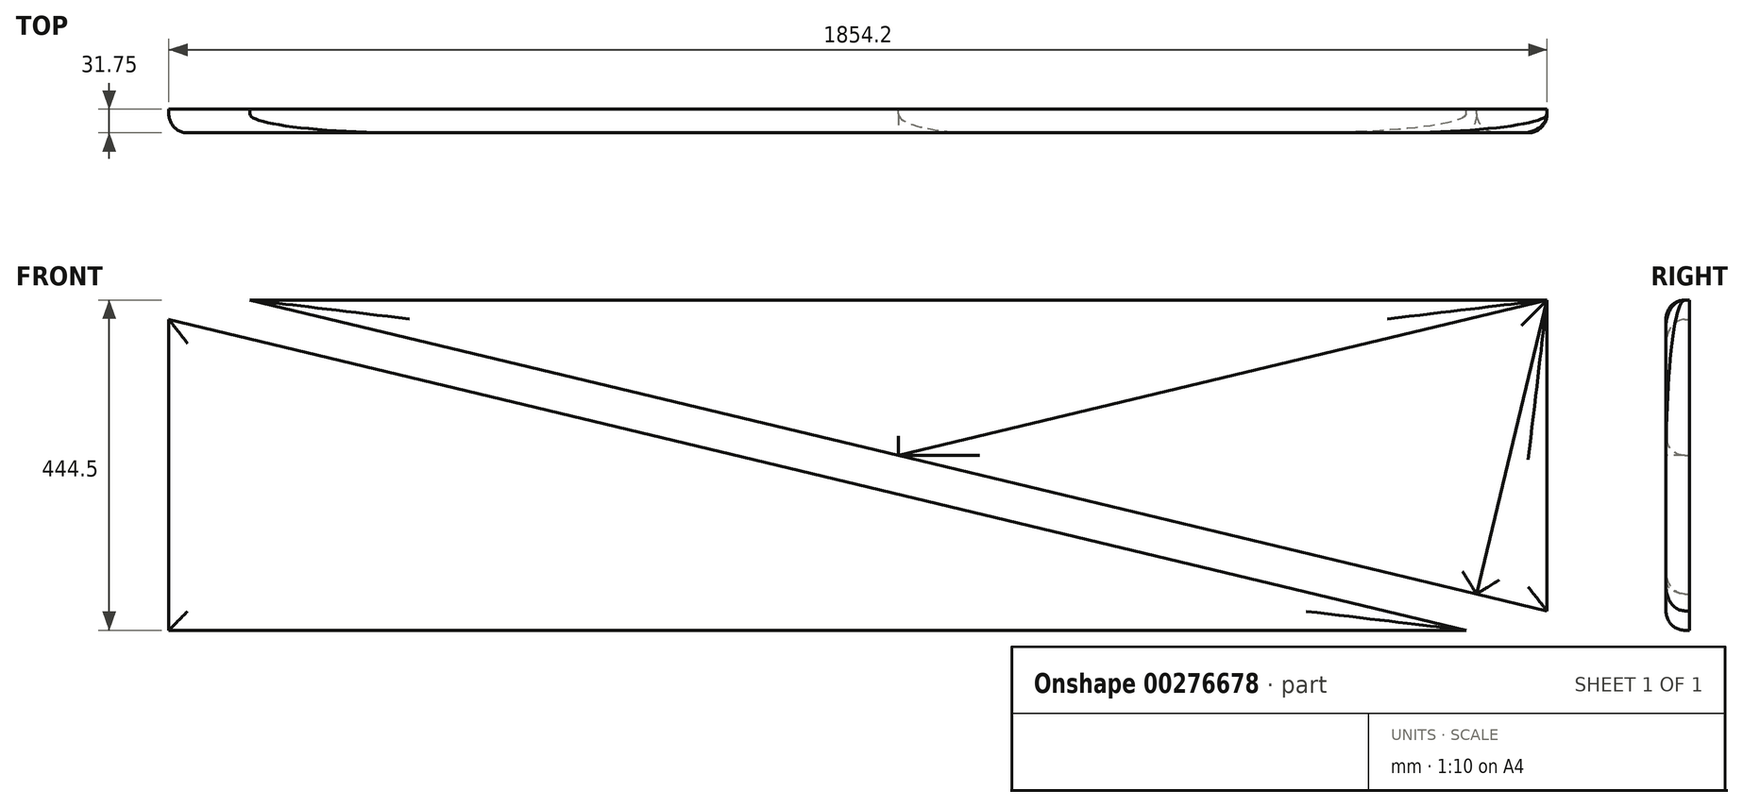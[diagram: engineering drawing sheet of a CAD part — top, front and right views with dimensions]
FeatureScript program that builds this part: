
annotation { "Feature Type Name" : "Feature", "Feature Type Description" : "" }
export const myFeature = defineFeature(function(context is Context, id is Id, definition is map)
    precondition{}
    {
        {
            var Q0;
            Q0=qCreatedBy(makeId("Front.planeOp"),FACE);
            var sketch = newSketch(context, id + "F0", { "sketchPlane" : qUnion([Q0])});
            skLineSegment(sketch, "E0.bottom", {"start": v(0, 0) * mm, "end": v(1854.2, 0) * mm});
            skLineSegment(sketch, "E0.top", {"start": v(0, 444.5) * mm, "end": v(1854.2, 444.5) * mm});
            skLineSegment(sketch, "E0.left", {"start": v(0, 0) * mm, "end": v(0, 444.5) * mm});
            skLineSegment(sketch, "E0.right", {"start": v(1854.2, 0) * mm, "end": v(1854.2, 444.5) * mm});
            skLineSegment(sketch, "E1", {"start": v(0, 444.5) * mm, "end": v(1854.2, 0) * mm});
            skLineSegment(sketch, "E2.0", {"start": v(0, 418.38) * mm, "end": v(1745.24, 0) * mm});
            skLineSegment(sketch, "E3.0", {"start": v(108.96, 444.5) * mm, "end": v(1854.2, 26.12) * mm});
            skLineSegment(sketch, "E4", {"start": v(1854.2, 444.5) * mm, "end": v(1759.35, 48.86) * mm});
            skLineSegment(sketch, "E5", {"start": v(1854.2, 444.5) * mm, "end": v(981.58, 235.3) * mm});
            skSolve(sketch);
        }
        {
            var Q0;
            {var subQ3=sQuery(id+"F0.wireOp",EDGE,"E2.0");Q0=makeQuery(id+"F0.imprint","IMPRINT",FACE,{"disambiguationData":[TD([[makeQuery(id+"F0.imprint","IMPRINT",EDGE,{"derivedFrom":subQ3}),-1.0]])]});}
            var Q1;
            {var subQ0=sQuery(id+"F0.wireOp",EDGE,"E5");Q1=makeQuery(id+"F0.imprint","IMPRINT",FACE,{"disambiguationData":[TD([[makeQuery(id+"F0.imprint","IMPRINT",EDGE,{"derivedFrom":subQ0}),-1.0]])]});}
            var Q2;
            {var subQ0=sQuery(id+"F0.wireOp",EDGE,"E4");Q2=makeQuery(id+"F0.imprint","IMPRINT",FACE,{"disambiguationData":[TD([[makeQuery(id+"F0.imprint","IMPRINT",EDGE,{"derivedFrom":subQ0}),1.0]])]});}
            extrude(context, id + "F1", {"entities" : qUnion([Q0, Q1, Q2]), "depth" : 31.75 * mm});
        }
        {
            var Q0;
            Q0=makeQuery(id+"F1.opExtrude","CAP_FACE",FACE,{"disambiguationData":[OSD([sQuery(id+"F0.wireOp",EDGE,"E0.bottom"),sQuery(id+"F0.wireOp",EDGE,"E0.left"),sQuery(id+"F0.wireOp",EDGE,"E2.0")])],"isStart":false});
            fillet(context, id + "F2", {"entities" : qUnion([Q0]), "radius" : 25.4 * mm, "tangentPropagation" : true, "allowEdgeOverflow" : false});
        }
        {
            var Q0;
            Q0=makeQuery(id+"F1.opExtrude","CAP_FACE",FACE,{"disambiguationData":[OSD([sQuery(id+"F0.wireOp",EDGE,"E0.top"),sQuery(id+"F0.wireOp",EDGE,"E3.0"),sQuery(id+"F0.wireOp",EDGE,"E5")])],"isStart":false});
            var Q1;
            Q1=makeQuery(id+"F1.opExtrude","CAP_FACE",FACE,{"disambiguationData":[OSD([sQuery(id+"F0.wireOp",EDGE,"E0.right"),sQuery(id+"F0.wireOp",EDGE,"E3.0"),sQuery(id+"F0.wireOp",EDGE,"E4")])],"isStart":false});
            fillet(context, id + "F3", {"entities" : qUnion([Q0, Q1]), "radius" : 25.4 * mm, "tangentPropagation" : true, "allowEdgeOverflow" : false});
        }
        {
            var Q0;
            {var subQ0=sQuery(id+"F0.wireOp",EDGE,"E4");Q0=makeQuery(id+"F0.imprint","IMPRINT",FACE,{"disambiguationData":[TD([[makeQuery(id+"F0.imprint","IMPRINT",EDGE,{"derivedFrom":subQ0}),-1.0]])]});}
            extrude(context, id + "F4", {"entities" : qUnion([Q0]), "depth" : 31.75 * mm});
        }
        {
            var Q0;
            Q0=makeQuery(id+"F4.opExtrude","CAP_FACE",FACE,{"disambiguationData":[OSD([sQuery(id+"F0.wireOp",EDGE,"E3.0"),sQuery(id+"F0.wireOp",EDGE,"E4"),sQuery(id+"F0.wireOp",EDGE,"E5")])],"isStart":false});
            fillet(context, id + "F5", {"entities" : qUnion([Q0]), "radius" : 25.4 * mm, "tangentPropagation" : true, "allowEdgeOverflow" : false});
        }
    });
